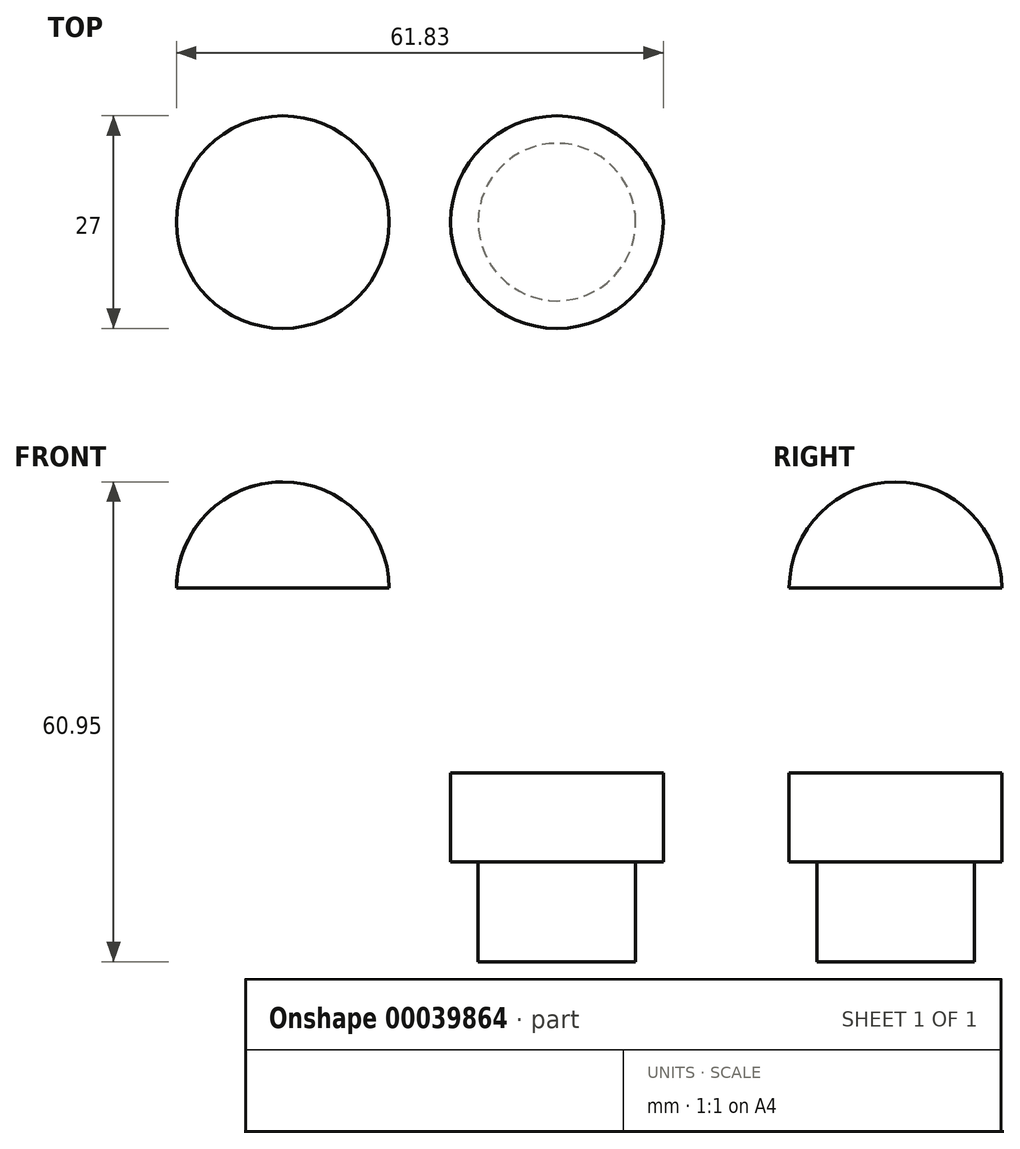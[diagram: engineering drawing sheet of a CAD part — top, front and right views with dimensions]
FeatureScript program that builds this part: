
annotation { "Feature Type Name" : "Feature", "Feature Type Description" : "" }
export const myFeature = defineFeature(function(context is Context, id is Id, definition is map)
    precondition{}
    {
        {
            var Q0;
            Q0=qCreatedBy(makeId("Top.planeOp"),FACE);
            var sketch = newSketch(context, id + "F0", { "sketchPlane" : qUnion([Q0])});
            skCircle(sketch, "E0", {"center": v(0, 0) * mm, "radius": 10 * mm});
            skSolve(sketch);
        }
        {
            var Q0;
            Q0=makeQuery(id+"F0.imprint","IMPRINT",FACE,{"disambiguationData":[TD([[makeQuery(id+"F0.imprint","IMPRINT",EDGE,{"derivedFrom":sQuery(id+"F0.wireOp",EDGE,"E0")}),1.0]])]});
            extrude(context, id + "F1", {"entities" : qUnion([Q0]), "depth" : 12.7 * mm});
        }
        {
            var Q0;
            Q0=makeQuery(id+"F1.opExtrude","CAP_FACE",FACE,{"disambiguationData":[OSD([sQuery(id+"F0.wireOp",EDGE,"E0")])],"isStart":false});
            var sketch = newSketch(context, id + "F2", { "sketchPlane" : qUnion([Q0])});
            skPoint(sketch, "E1", {"position": v(0, 0) * mm});
            skCircle(sketch, "E2", {"center": v(0, 0) * mm, "radius": 13.5 * mm});
            skSolve(sketch);
        }
        {
            var Q0;
            Q0=makeQuery(id+"F2.imprint","IMPRINT",FACE,{"disambiguationData":[TD([[makeQuery(id+"F2.imprint","IMPRINT",EDGE,{"derivedFrom":makeQuery(id+"F1.opExtrude","CAP_EDGE",EDGE,{"disambiguationData":[OSD([sQuery(id+"F0.wireOp",EDGE,"E0")])],"isStart":false})}),1.0]])]});
            extrude(context, id + "F3", {"entities" : qUnion([Q0]), "operationType" : NewBodyOperationType.ADD, "depth" : 11.3 * mm});
        }
        {
            var Q0;
            Q0=makeQuery(id+"F2.imprint","IMPRINT",FACE,{"disambiguationData":[TD([[makeQuery(id+"F2.imprint","IMPRINT",EDGE,{"derivedFrom":sQuery(id+"F2.wireOp",EDGE,"E2")}),1.0]])]});
            var Q1;
            Q1=makeQuery(id+"F3.opExtrude","CAP_FACE",FACE,{"disambiguationData":[OSD([sQuery(id+"F0.wireOp",EDGE,"E0")])],"isStart":false});
            extrude(context, id + "F4", {"entities" : qUnion([Q0]), "operationType" : NewBodyOperationType.ADD, "endBound" : BoundingType.UP_TO_SURFACE, "endBoundEntityFace" : qUnion([Q1]), "depth" : 9.76 * mm});
        }
        {
            var Q0;
            {var subQ0=sQuery(id+"F0.wireOp",EDGE,"E0");Q0=makeQuery(id+"F4.boolean.opBoolean","MERGE",FACE,{"derivedFrom":[makeQuery(id+"F3.opExtrude","CAP_FACE",FACE,{"disambiguationData":[OSD([subQ0])],"isStart":false}),makeQuery(id+"F4.opExtrude","CAP_FACE",FACE,{"disambiguationData":[OSD([subQ0,sQuery(id+"F2.wireOp",EDGE,"E2")])],"isStart":false})]});}
            var sketch = newSketch(context, id + "F5", { "sketchPlane" : qUnion([Q0])});
            skPoint(sketch, "E3", {"position": v(0, 0) * mm});
            skSolve(sketch);
        }
        {
            var Q0;
            Q0=qCreatedBy(makeId("Front.planeOp"),FACE);
            var sketch = newSketch(context, id + "F6", { "sketchPlane" : qUnion([Q0])});
            skLineSegment(sketch, "E4", {"start": v(-34.83, 47.45) * mm, "end": v(-48.33, 47.45) * mm});
            skLineSegment(sketch, "E5", {"start": v(-34.83, 47.45) * mm, "end": v(-34.83, 60.95) * mm});
            skArc(sketch, "E6", {"start": v(-48.33, 47.45) * mm, "mid": v(-44.37, 57) * mm, "end": v(-34.83, 60.95) * mm});
            skSolve(sketch);
        }
        {
            var Q0;
            Q0 = qSketchRegion(id + "F6", true);
            var Q1;
            Q1=sQuery(id+"F6.wireOp",EDGE,"E5");
            revolve(context, id + "F7", {"entities" : qUnion([Q0]), "axis" : qUnion([Q1]), "revolveType" : RevolveType.FULL});
        }
    });
